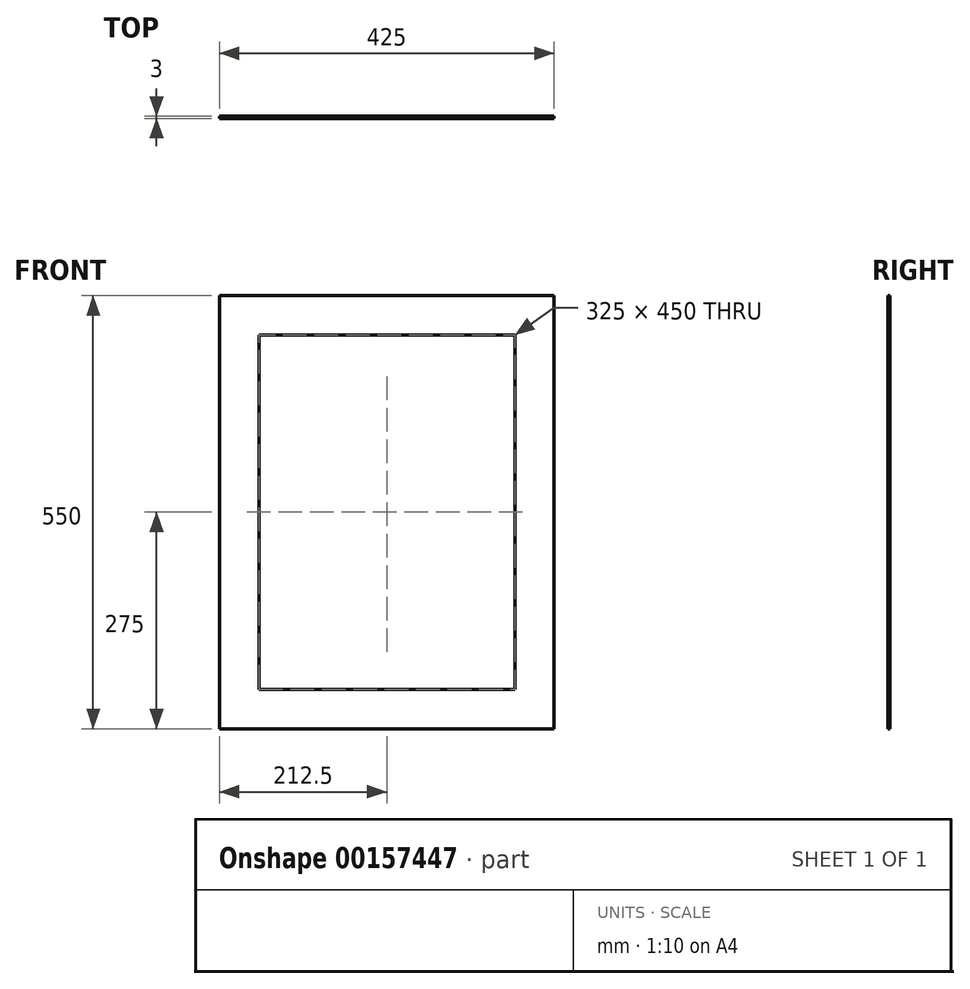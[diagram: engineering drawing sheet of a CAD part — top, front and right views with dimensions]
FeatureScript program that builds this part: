
annotation { "Feature Type Name" : "Feature", "Feature Type Description" : "" }
export const myFeature = defineFeature(function(context is Context, id is Id, definition is map)
    precondition{}
    {
        {
            var Q0;
            Q0=qCreatedBy(makeId("Front.planeOp"),FACE);
            var sketch = newSketch(context, id + "F0", { "sketchPlane" : qUnion([Q0])});
            skLineSegment(sketch, "E0.bottom", {"start": v(212.5, -275) * mm, "end": v(-212.5, -275) * mm});
            skLineSegment(sketch, "E0.top", {"start": v(212.5, 275) * mm, "end": v(-212.5, 275) * mm});
            skLineSegment(sketch, "E0.left", {"start": v(212.5, -275) * mm, "end": v(212.5, 275) * mm});
            skLineSegment(sketch, "E0.right", {"start": v(-212.5, -275) * mm, "end": v(-212.5, 275) * mm});
            skPoint(sketch, "E0.middle", {"position": v(0, 0) * mm});
            skLineSegment(sketch, "E1.bottom", {"start": v(162.5, -225) * mm, "end": v(-162.5, -225) * mm});
            skLineSegment(sketch, "E1.top", {"start": v(162.5, 225) * mm, "end": v(-162.5, 225) * mm});
            skLineSegment(sketch, "E1.left", {"start": v(162.5, -225) * mm, "end": v(162.5, 225) * mm});
            skLineSegment(sketch, "E1.right", {"start": v(-162.5, -225) * mm, "end": v(-162.5, 225) * mm});
            skSolve(sketch);
        }
        {
            var Q0;
            Q0=makeQuery(id+"F0.imprint","IMPRINT",FACE,{"disambiguationData":[TD([[makeQuery(id+"F0.imprint","IMPRINT",EDGE,{"derivedFrom":sQuery(id+"F0.wireOp",EDGE,"E0.bottom")}),-1.0]])]});
            extrude(context, id + "F1", {"entities" : qUnion([Q0]), "depth" : 3 * mm});
        }
    });
